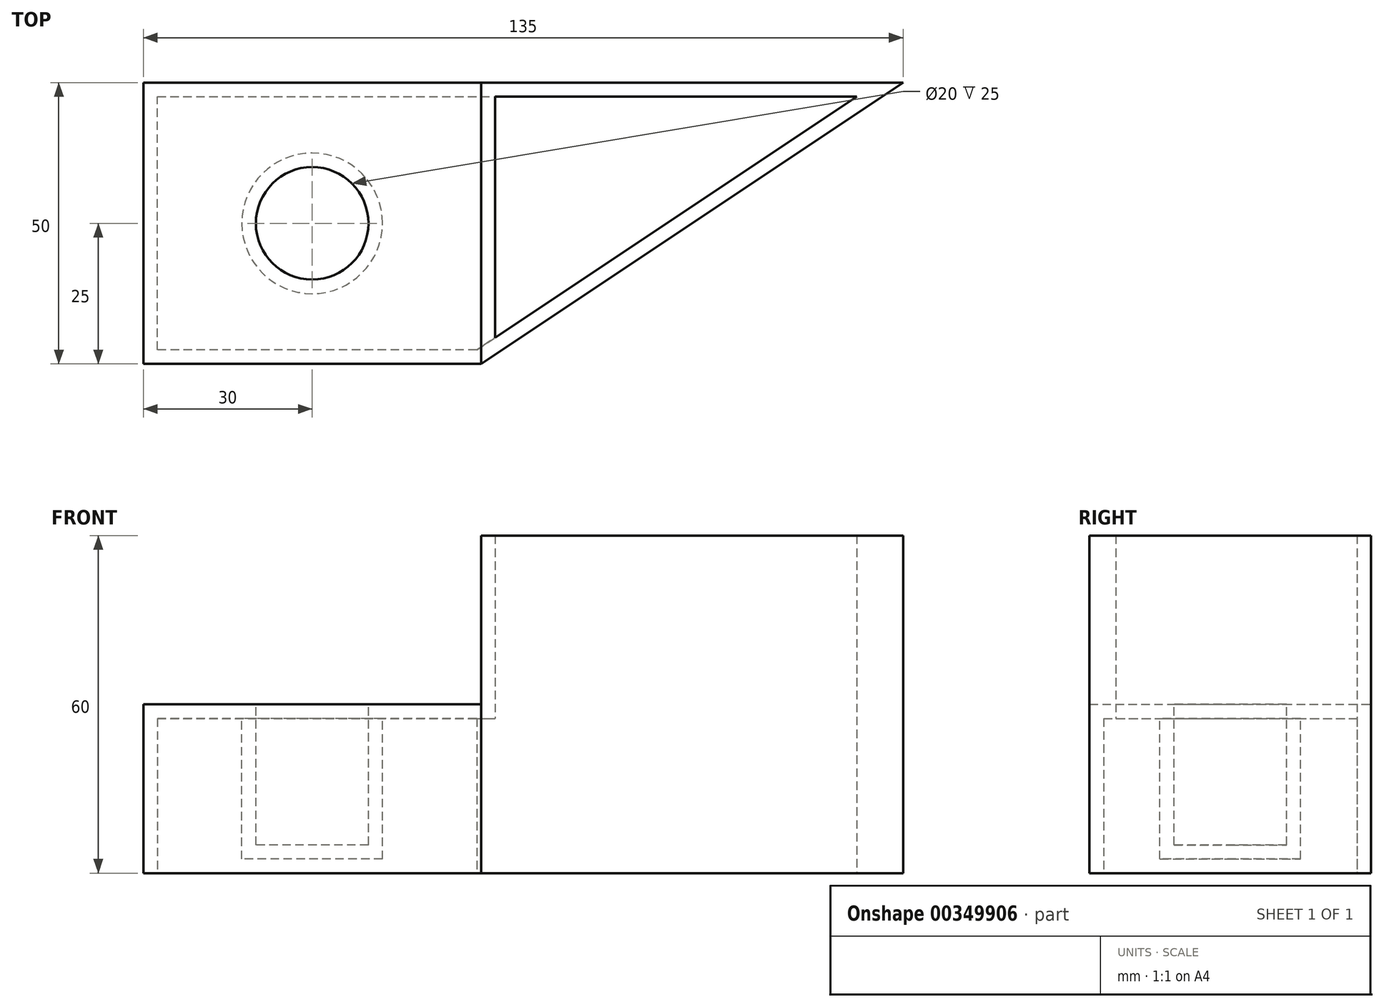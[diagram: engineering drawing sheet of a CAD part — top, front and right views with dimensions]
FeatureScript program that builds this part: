
annotation { "Feature Type Name" : "Feature", "Feature Type Description" : "" }
export const myFeature = defineFeature(function(context is Context, id is Id, definition is map)
    precondition{}
    {
        {
            var Q0;
            Q0=qCreatedBy(makeId("Top.planeOp"),FACE);
            var sketch = newSketch(context, id + "F0", { "sketchPlane" : qUnion([Q0])});
            skLineSegment(sketch, "E0", {"start": v(0, 0) * mm, "end": v(0, 50) * mm});
            skLineSegment(sketch, "E1", {"start": v(0, 50) * mm, "end": v(75, 50) * mm});
            skLineSegment(sketch, "E2", {"start": v(75, 50) * mm, "end": v(0, 0) * mm});
            skLineSegment(sketch, "E3", {"start": v(0, 0) * mm, "end": v(-60, 0) * mm});
            skLineSegment(sketch, "E4", {"start": v(-60, 0) * mm, "end": v(-60, 50) * mm});
            skLineSegment(sketch, "E5", {"start": v(-60, 50) * mm, "end": v(0, 50) * mm});
            skSolve(sketch);
        }
        {
            var Q0;
            Q0=makeQuery(id+"F0.imprint","IMPRINT",FACE,{"disambiguationData":[TD([[makeQuery(id+"F0.imprint","IMPRINT",EDGE,{"derivedFrom":sQuery(id+"F0.wireOp",EDGE,"E0")}),1.0]])]});
            extrude(context, id + "F1", {"entities" : qUnion([Q0]), "depth" : 30 * mm});
        }
        {
            var Q0;
            Q0=makeQuery(id+"F0.imprint","IMPRINT",FACE,{"disambiguationData":[TD([[makeQuery(id+"F0.imprint","IMPRINT",EDGE,{"derivedFrom":sQuery(id+"F0.wireOp",EDGE,"E0")}),-1.0]])]});
            extrude(context, id + "F2", {"entities" : qUnion([Q0]), "operationType" : NewBodyOperationType.ADD, "depth" : 60 * mm});
        }
        {
            var Q0;
            Q0=makeQuery(id+"F1.opExtrude","CAP_FACE",FACE,{"disambiguationData":[OSD([sQuery(id+"F0.wireOp",EDGE,"E0"),sQuery(id+"F0.wireOp",EDGE,"E3"),sQuery(id+"F0.wireOp",EDGE,"E4"),sQuery(id+"F0.wireOp",EDGE,"E5")])],"isStart":false});
            var sketch = newSketch(context, id + "F3", { "sketchPlane" : qUnion([Q0])});
            skLineSegment(sketch, "E6", {"start": v(0, 50) * mm, "end": v(-60, 0) * mm});
            skCircle(sketch, "E7", {"center": v(-30, 25) * mm, "radius": 10 * mm});
            skSolve(sketch);
        }
        {
            var Q0;
            {var subQ0=sQuery(id+"F3.wireOp",EDGE,"E7");var subQ1=sQuery(id+"F3.wireOp",EDGE,"E6");var subQ2=makeQuery(id+"F3.imprint","INTERSECT",VERTEX,{"disambiguationData":[OD(0.0)],"derivedFrom":[subQ1,subQ0]});Q0=makeQuery(id+"F3.imprint","IMPRINT",FACE,{"disambiguationData":[TD([[makeQuery(id+"F3.imprint","IMPRINT",EDGE,{"disambiguationData":[TD([[subQ2,-1.0]])],"derivedFrom":subQ1}),1.0]])]});}
            var Q1;
            {var subQ0=sQuery(id+"F3.wireOp",EDGE,"E7");var subQ1=sQuery(id+"F3.wireOp",EDGE,"E6");var subQ2=makeQuery(id+"F3.imprint","INTERSECT",VERTEX,{"disambiguationData":[OD(0.0)],"derivedFrom":[subQ1,subQ0]});Q1=makeQuery(id+"F3.imprint","IMPRINT",FACE,{"disambiguationData":[TD([[makeQuery(id+"F3.imprint","IMPRINT",EDGE,{"disambiguationData":[TD([[subQ2,-1.0]])],"derivedFrom":subQ1}),-1.0]])]});}
            extrude(context, id + "F4", {"entities" : qUnion([Q0, Q1]), "operationType" : NewBodyOperationType.REMOVE, "oppositeDirection" : true, "depth" : 25 * mm});
        }
        {
            var Q0;
            Q0=makeQuery(id+"F2.opExtrude","CAP_FACE",FACE,{"disambiguationData":[OSD([sQuery(id+"F0.wireOp",EDGE,"E0"),sQuery(id+"F0.wireOp",EDGE,"E1"),sQuery(id+"F0.wireOp",EDGE,"E2")])],"isStart":false});
            var Q1;
            {var subQ0=sQuery(id+"F0.wireOp",EDGE,"E0");Q1=makeQuery(id+"F2.boolean.opBoolean","MERGE",FACE,{"derivedFrom":[makeQuery(id+"F1.opExtrude","CAP_FACE",FACE,{"disambiguationData":[OSD([subQ0,sQuery(id+"F0.wireOp",EDGE,"E3"),sQuery(id+"F0.wireOp",EDGE,"E4"),sQuery(id+"F0.wireOp",EDGE,"E5")])],"isStart":true}),makeQuery(id+"F2.opExtrude","CAP_FACE",FACE,{"disambiguationData":[OSD([subQ0,sQuery(id+"F0.wireOp",EDGE,"E1"),sQuery(id+"F0.wireOp",EDGE,"E2")])],"isStart":true})]});}
            shell(context, id + "F5", {"entities" : qUnion([Q0, Q1]), "thickness" : 2.5 * mm});
        }
    });
